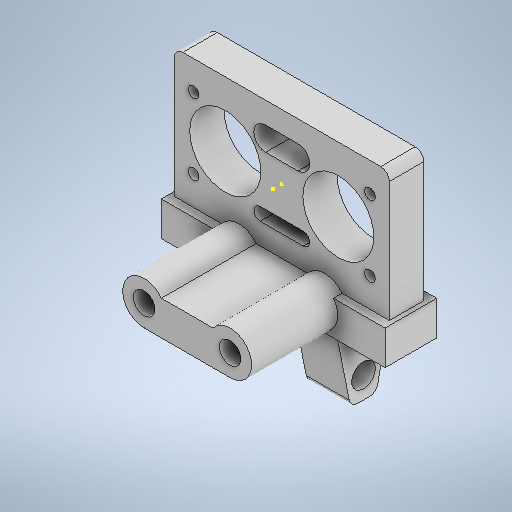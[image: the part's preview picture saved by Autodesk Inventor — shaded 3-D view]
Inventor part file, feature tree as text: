
AUTODESK INVENTOR PART (.ipt)
format: ipt  version: 2025.2 (Build 292293000, 293)  size: 428,544 bytes
history: native  units: mm
features: sketch x13, extrude x10, mirror x3, fillet x2, other x1, hole x1
ambient origin geometry x8: Origin, YZ Plane, XZ Plane, XY Plane, X Axis, Y Axis, Z Axis, Center Point
bodies: Body1 (feature_tree)
feature tree (30):
  other  "Bryła1"
  extrude  "Wyciągnięcie proste1"  Depth=50.0mm
  hole  "Otwór2"  [1 undecoded]
  extrude  "Wyciągnięcie proste3"  Depth=8.0mm TaperAngle=0.0deg
  mirror  "Odbij1"
  extrude  "Wyciągnięcie proste4"  Depth=41.0mm
  fillet  "Zaokrąglenie1"  Radius=16.5mm
  extrude  "Wyciągnięcie proste5"  Depth=45.0mm
  extrude  "Wyciągnięcie proste6"  Depth=20.0mm
  extrude  "Wyciągnięcie proste7"  Depth=16.5mm
  extrude  "Wyciągnięcie proste8"  Depth=9.35mm
  extrude  "Wyciągnięcie proste9"  Depth=10.0mm
  fillet  "Zaokrąglenie2"  Radius=8.0mm
  mirror  "Odbij2"
  extrude  "Wyciągnięcie proste13"  Depth=45.0mm
  sketch  "Szkic23"
  sketch  "Szkic24"
  extrude  "Wyciągnięcie proste14"  Depth=20.0mm
  mirror  "Odbij4"
  sketch  "Szkic1"
  sketch  "Szkic8"
  sketch  "Szkic9"
  sketch  "Szkic10"
  sketch  "Szkic11"
  sketch  "Szkic13"
  sketch  "Szkic14"
  sketch  "Szkic15"
  sketch  "Szkic16"
  sketch  "Szkic22"
  sketch  "Szkic25"
note: 1 required parameter value undecoded (feature->parameter linkage not recoverable at this tier; creation-order binding heuristic only, values carry confidence <= 0.55)
